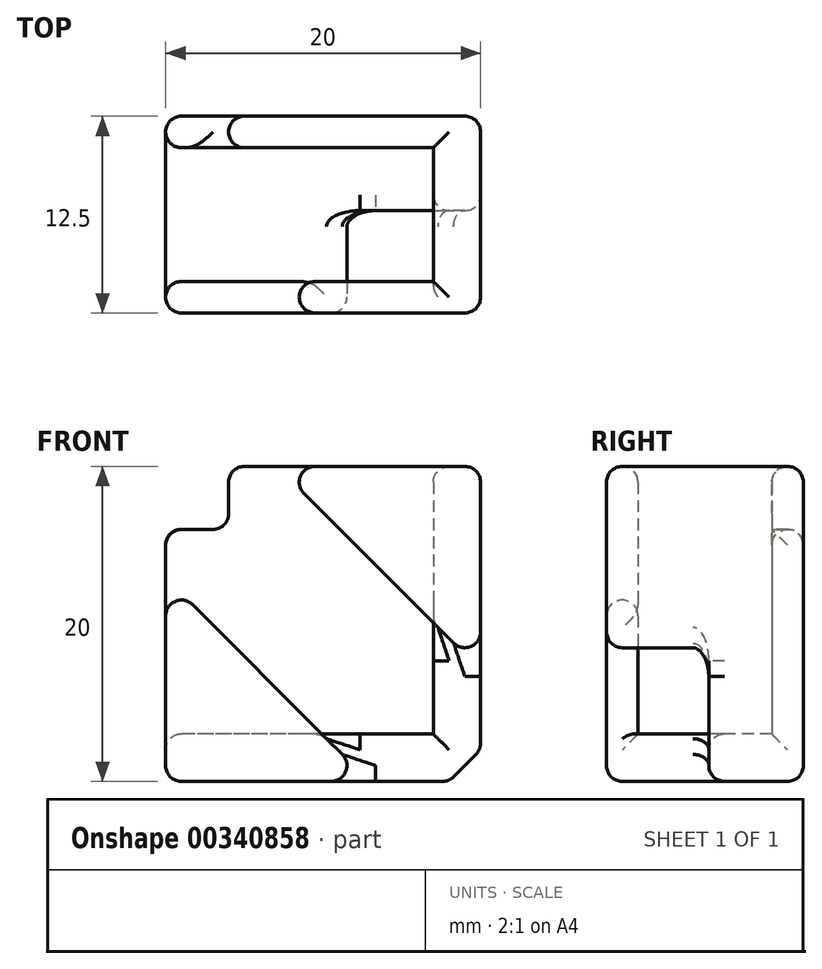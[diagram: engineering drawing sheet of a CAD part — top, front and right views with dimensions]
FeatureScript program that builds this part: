
annotation { "Feature Type Name" : "Feature", "Feature Type Description" : "" }
export const myFeature = defineFeature(function(context is Context, id is Id, definition is map)
    precondition{}
    {
        {
            var Q0;
            Q0=qCreatedBy(makeId("Top.planeOp"),FACE);
            var sketch = newSketch(context, id + "F0", { "sketchPlane" : qUnion([Q0])});
            skLineSegment(sketch, "E0.bottom", {"start": v(0, 0) * mm, "end": v(20, 0) * mm});
            skLineSegment(sketch, "E0.top", {"start": v(0, -12.5) * mm, "end": v(20, -12.5) * mm});
            skLineSegment(sketch, "E0.left", {"start": v(0, 0) * mm, "end": v(0, -12.5) * mm});
            skLineSegment(sketch, "E0.right", {"start": v(20, 0) * mm, "end": v(20, -12.5) * mm});
            skLineSegment(sketch, "E1.bottom", {"start": v(0, -2) * mm, "end": v(20, -2) * mm});
            skLineSegment(sketch, "E1.top", {"start": v(0, -10.5) * mm, "end": v(20, -10.5) * mm});
            skLineSegment(sketch, "E1.left", {"start": v(0, -2) * mm, "end": v(0, -10.5) * mm});
            skLineSegment(sketch, "E1.right", {"start": v(20, -2) * mm, "end": v(20, -10.5) * mm});
            skSolve(sketch);
        }
        {
            var Q0;
            Q0=qSketchRegion(id+"F0",true);
            extrude(context, id + "F1", {"entities" : qUnion([Q0]), "depth" : 3 * mm});
        }
        {
            var Q0;
            {var subQ0=sQuery(id+"F0.wireOp",EDGE,"E0.bottom");Q0=makeQuery(id+"F0.imprint","IMPRINT",FACE,{"disambiguationData":[TD([[makeQuery(id+"F0.imprint","IMPRINT",EDGE,{"derivedFrom":subQ0}),-1.0]])]});}
            var Q1;
            {var subQ0=sQuery(id+"F0.wireOp",EDGE,"E0.top");Q1=makeQuery(id+"F0.imprint","IMPRINT",FACE,{"disambiguationData":[TD([[makeQuery(id+"F0.imprint","IMPRINT",EDGE,{"derivedFrom":subQ0}),1.0]])]});}
            extrude(context, id + "F2", {"entities" : qUnion([Q0, Q1]), "operationType" : NewBodyOperationType.ADD, "depth" : 16 * mm});
        }
        {
            var Q0;
            Q0=makeQuery(id+"F1.opExtrude","SWEPT_BODY",BODY,{"disambiguationData":[OSD([sQuery(id+"F0.wireOp",EDGE,"E0.bottom"),sQuery(id+"F0.wireOp",EDGE,"E0.top"),sQuery(id+"F0.wireOp",EDGE,"E0.left"),sQuery(id+"F0.wireOp",EDGE,"E0.right"),sQuery(id+"F0.wireOp",EDGE,"E1.left"),sQuery(id+"F0.wireOp",EDGE,"E1.right")])]});
            var Q1;
            Q1=sQuery(id+"F0.wireOp",EDGE,"E1.left");
            transform(context, id + "F3", {"entities" : qUnion([Q0]), "transformType" : TransformType.ROTATION, "transformAxis" : qUnion([Q1]), "angle" : 90 * degree, "makeCopy" : true});
        }
        {
            var Q0;
            Q0=makeQuery(id+"F3.opPattern","COPY",BODY,{"derivedFrom":makeQuery(id+"F1.opExtrude","SWEPT_BODY",BODY,{"disambiguationData":[OSD([sQuery(id+"F0.wireOp",EDGE,"E0.bottom"),sQuery(id+"F0.wireOp",EDGE,"E0.top"),sQuery(id+"F0.wireOp",EDGE,"E0.left"),sQuery(id+"F0.wireOp",EDGE,"E0.right"),sQuery(id+"F0.wireOp",EDGE,"E1.left"),sQuery(id+"F0.wireOp",EDGE,"E1.right")])]}),"instanceName":"1"});
            var Q1;
            {var subQ0=sQuery(id+"F0.wireOp",EDGE,"E0.bottom");Q1=makeQuery(id+"FWMDLX0BPGAaUFk_1.opFillet","BLEND_EDGE",EDGE,{"blendedFrom":[makeQuery(id+"F1.opExtrude","CAP_EDGE",EDGE,{"disambiguationData":[OSD([subQ0])],"isStart":true}),makeQuery(id+"F1.opExtrude","CAP_FACE",FACE,{"disambiguationData":[OSD([subQ0,sQuery(id+"F0.wireOp",EDGE,"E0.top"),sQuery(id+"F0.wireOp",EDGE,"E0.left"),sQuery(id+"F0.wireOp",EDGE,"E0.right"),sQuery(id+"F0.wireOp",EDGE,"E1.left"),sQuery(id+"F0.wireOp",EDGE,"E1.right")])],"isStart":true})],"blendedInto":[makeQuery(id+"F1.opExtrude","CAP_FACE",FACE,{"disambiguationData":[OSD([subQ0,sQuery(id+"F0.wireOp",EDGE,"E0.top"),sQuery(id+"F0.wireOp",EDGE,"E0.left"),sQuery(id+"F0.wireOp",EDGE,"E0.right"),sQuery(id+"F0.wireOp",EDGE,"E1.left"),sQuery(id+"F0.wireOp",EDGE,"E1.right")])],"isStart":true})]});}
            transform(context, id + "F4", {"entities" : qUnion([Q0]), "transformType" : TransformType.TRANSLATION_3D, "dx" : 20 * mm, "dy" : 0 * mm, "dz" : 0 * mm, "makeCopy" : false});
        }
        {
            var Q0;
            Q0=makeQuery(id+"F1.opExtrude","SWEPT_BODY",BODY,{"disambiguationData":[OSD([sQuery(id+"F0.wireOp",EDGE,"E0.bottom"),sQuery(id+"F0.wireOp",EDGE,"E0.top"),sQuery(id+"F0.wireOp",EDGE,"E0.left"),sQuery(id+"F0.wireOp",EDGE,"E0.right"),sQuery(id+"F0.wireOp",EDGE,"E1.left"),sQuery(id+"F0.wireOp",EDGE,"E1.right")])]});
            var Q1;
            Q1=makeQuery(id+"F3.opPattern","COPY",BODY,{"derivedFrom":makeQuery(id+"F1.opExtrude","SWEPT_BODY",BODY,{"disambiguationData":[OSD([sQuery(id+"F0.wireOp",EDGE,"E0.bottom"),sQuery(id+"F0.wireOp",EDGE,"E0.top"),sQuery(id+"F0.wireOp",EDGE,"E0.left"),sQuery(id+"F0.wireOp",EDGE,"E0.right"),sQuery(id+"F0.wireOp",EDGE,"E1.left"),sQuery(id+"F0.wireOp",EDGE,"E1.right")])]}),"instanceName":"1"});
            booleanBodies(context, id + "F5", {"operationType" : BooleanOperationType.UNION, "tools" : qUnion([Q0, Q1])});
        }
        {
            var Q0;
            {var subQ0=sQuery(id+"F0.wireOp",EDGE,"E0.top");var subQ1=makeQuery(id+"F2.boolean.opBoolean","MERGE",FACE,{"derivedFrom":[makeQuery(id+"F1.opExtrude","SWEPT_FACE",FACE,{"disambiguationData":[OSD([subQ0])]}),makeQuery(id+"F2.opExtrude","SWEPT_FACE",FACE,{"disambiguationData":[OSD([subQ0])]})]});Q0=makeQuery(id+"F5.opBoolean","MERGE",FACE,{"derivedFrom":[subQ1,makeQuery(id+"F3.opPattern","COPY",FACE,{"derivedFrom":subQ1,"instanceName":"1"})]});}
            var sketch = newSketch(context, id + "F6", { "sketchPlane" : qUnion([Q0])});
            skPoint(sketch, "E2", {"position": v(10, 1) * mm});
            skPoint(sketch, "E3", {"position": v(19, 10) * mm});
            skLineSegment(sketch, "E4", {"start": v(3.97, 23.1) * mm, "end": v(-3.1, 16.03) * mm});
            skLineSegment(sketch, "E5", {"start": v(17.25, -4.32) * mm, "end": v(24.32, 2.75) * mm});
            skLineSegment(sketch, "E6", {"start": v(17.25, -4.32) * mm, "end": v(-3.1, 16.03) * mm});
            skLineSegment(sketch, "E7", {"start": v(24.32, 2.75) * mm, "end": v(3.97, 23.1) * mm});
            skSolve(sketch);
        }
        {
            var Q0;
            Q0 = qSketchRegion(id + "F6", true);
            extrude(context, id + "F7", {"entities" : qUnion([Q0]), "operationType" : NewBodyOperationType.REMOVE, "oppositeDirection" : true, "depth" : 6.5 * mm});
        }
        {
            var Q0;
            Q0=makeQuery(id+"F1.opExtrude","CAP_EDGE",EDGE,{"disambiguationData":[OSD([sQuery(id+"F0.wireOp",EDGE,"E0.right"),sQuery(id+"F0.wireOp",EDGE,"E1.right")])],"isStart":true});
            chamfer(context, id + "F8", {"entities" : qUnion([Q0]), "width" : 2 * mm, "tangentPropagation" : true});
        }
        {
            var Q0;
            {var subQ0=sQuery(id+"F0.wireOp",EDGE,"E0.bottom");var subQ1=makeQuery(id+"F2.boolean.opBoolean","MERGE",FACE,{"derivedFrom":[makeQuery(id+"F1.opExtrude","SWEPT_FACE",FACE,{"disambiguationData":[OSD([subQ0])]}),makeQuery(id+"F2.opExtrude","SWEPT_FACE",FACE,{"disambiguationData":[OSD([subQ0])]})]});Q0=makeQuery(id+"F5.opBoolean","MERGE",FACE,{"derivedFrom":[subQ1,makeQuery(id+"F3.opPattern","COPY",FACE,{"derivedFrom":subQ1,"instanceName":"1"})]});}
            var Q1;
            Q1=makeQuery(id+"F1.opExtrude","CAP_FACE",FACE,{"disambiguationData":[OSD([sQuery(id+"F0.wireOp",EDGE,"E0.bottom"),sQuery(id+"F0.wireOp",EDGE,"E0.top"),sQuery(id+"F0.wireOp",EDGE,"E0.left"),sQuery(id+"F0.wireOp",EDGE,"E0.right"),sQuery(id+"F0.wireOp",EDGE,"E1.left"),sQuery(id+"F0.wireOp",EDGE,"E1.right")])],"isStart":true});
            var Q2;
            {var subQ0=sQuery(id+"F0.wireOp",EDGE,"E1.right");var subQ1=sQuery(id+"F0.wireOp",EDGE,"E0.right");var subQ2=sQuery(id+"F0.wireOp",EDGE,"E0.top");var subQ3=sQuery(id+"F0.wireOp",EDGE,"E0.bottom");Q2=makeQuery(id+"F5.opBoolean","MERGE",FACE,{"derivedFrom":[makeQuery(id+"F2.boolean.opBoolean","MERGE",FACE,{"derivedFrom":[makeQuery(id+"F1.opExtrude","SWEPT_FACE",FACE,{"disambiguationData":[OSD([subQ1,subQ0])]}),makeQuery(id+"F2.opExtrude","SWEPT_FACE",FACE,{"disambiguationData":[OSD([subQ1]),TDD([makeQuery(id+"F0.imprint","IMPRINT",EDGE,{"disambiguationData":[TD([[makeQuery(id+"F0.imprint","INTERSECT",VERTEX,{"derivedFrom":[subQ3,subQ1]}),-1.0]])],"derivedFrom":subQ1})])]}),makeQuery(id+"F2.opExtrude","SWEPT_FACE",FACE,{"disambiguationData":[OSD([subQ1]),TDD([makeQuery(id+"F0.imprint","IMPRINT",EDGE,{"disambiguationData":[TD([[makeQuery(id+"F0.imprint","INTERSECT",VERTEX,{"derivedFrom":[subQ2,subQ1]}),1.0]])],"derivedFrom":subQ1})])]})]}),makeQuery(id+"F3.opPattern","COPY",FACE,{"derivedFrom":makeQuery(id+"F1.opExtrude","CAP_FACE",FACE,{"disambiguationData":[OSD([subQ3,subQ2,sQuery(id+"F0.wireOp",EDGE,"E0.left"),subQ1,sQuery(id+"F0.wireOp",EDGE,"E1.left"),subQ0])],"isStart":true}),"instanceName":"1"})]});}
            var Q3;
            Q3=makeQuery(id+"F7.boolean.opBoolean","COPY",FACE,{"derivedFrom":makeQuery(id+"F7.opExtrude","CAP_FACE",FACE,{"disambiguationData":[OSD([sQuery(id+"F6.wireOp",EDGE,"E4"),sQuery(id+"F6.wireOp",EDGE,"E5"),sQuery(id+"F6.wireOp",EDGE,"E6"),sQuery(id+"F6.wireOp",EDGE,"E7")])],"isStart":false})});
            var Q4;
            Q4=makeQuery(id+"F7.boolean.opBoolean","COPY",FACE,{"derivedFrom":makeQuery(id+"F7.opExtrude","SWEPT_FACE",FACE,{"disambiguationData":[OSD([sQuery(id+"F6.wireOp",EDGE,"E6")])]})});
            var Q5;
            {var subQ0=sQuery(id+"F0.wireOp",EDGE,"E0.left");var subQ1=sQuery(id+"F0.wireOp",EDGE,"E1.left");Q5=makeQuery(id+"F2.boolean.opBoolean","MERGE",FACE,{"derivedFrom":[makeQuery(id+"F1.opExtrude","SWEPT_FACE",FACE,{"disambiguationData":[OSD([subQ0,subQ1])]}),makeQuery(id+"F2.opExtrude","SWEPT_FACE",FACE,{"disambiguationData":[OSD([subQ0]),TDD([makeQuery(id+"F0.imprint","IMPRINT",EDGE,{"disambiguationData":[TD([[makeQuery(id+"F0.imprint","INTERSECT",VERTEX,{"derivedFrom":[sQuery(id+"F0.wireOp",EDGE,"E0.bottom"),subQ0]}),-1.0]])],"derivedFrom":subQ0})])]}),makeQuery(id+"F2.opExtrude","SWEPT_FACE",FACE,{"disambiguationData":[OSD([subQ0]),TDD([makeQuery(id+"F0.imprint","IMPRINT",EDGE,{"disambiguationData":[TD([[makeQuery(id+"F0.imprint","INTERSECT",VERTEX,{"derivedFrom":[sQuery(id+"F0.wireOp",EDGE,"E0.top"),subQ0]}),1.0]])],"derivedFrom":subQ0})])]})]});}
            var Q6;
            {var subQ0=sQuery(id+"F0.wireOp",EDGE,"E0.right");var subQ1=sQuery(id+"F0.wireOp",EDGE,"E1.right");Q6=makeQuery(id+"F3.opPattern","COPY",FACE,{"derivedFrom":makeQuery(id+"F2.boolean.opBoolean","MERGE",FACE,{"derivedFrom":[makeQuery(id+"F1.opExtrude","SWEPT_FACE",FACE,{"disambiguationData":[OSD([subQ0,subQ1])]}),makeQuery(id+"F2.opExtrude","SWEPT_FACE",FACE,{"disambiguationData":[OSD([subQ0]),TDD([makeQuery(id+"F0.imprint","IMPRINT",EDGE,{"disambiguationData":[TD([[makeQuery(id+"F0.imprint","INTERSECT",VERTEX,{"derivedFrom":[sQuery(id+"F0.wireOp",EDGE,"E0.bottom"),subQ0]}),-1.0]])],"derivedFrom":subQ0})])]}),makeQuery(id+"F2.opExtrude","SWEPT_FACE",FACE,{"disambiguationData":[OSD([subQ0]),TDD([makeQuery(id+"F0.imprint","IMPRINT",EDGE,{"disambiguationData":[TD([[makeQuery(id+"F0.imprint","INTERSECT",VERTEX,{"derivedFrom":[sQuery(id+"F0.wireOp",EDGE,"E0.top"),subQ0]}),1.0]])],"derivedFrom":subQ0})])]})]}),"instanceName":"1"});}
            var Q7;
            Q7=makeQuery(id+"F7.boolean.opBoolean","COPY",FACE,{"derivedFrom":makeQuery(id+"F7.opExtrude","SWEPT_FACE",FACE,{"disambiguationData":[OSD([sQuery(id+"F6.wireOp",EDGE,"E7")])]})});
            var Q8;
            Q8=makeQuery(id+"F3.opPattern","COPY",FACE,{"derivedFrom":makeQuery(id+"F2.opExtrude","CAP_FACE",FACE,{"disambiguationData":[OSD([sQuery(id+"F0.wireOp",EDGE,"E0.bottom"),sQuery(id+"F0.wireOp",EDGE,"E0.left"),sQuery(id+"F0.wireOp",EDGE,"E0.right"),sQuery(id+"F0.wireOp",EDGE,"E1.bottom")])],"isStart":false}),"instanceName":"1"});
            fillet(context, id + "F9", {"entities" : qUnion([Q0, Q1, Q2, Q3, Q4, Q5, Q6, Q7, Q8]), "radius" : 1 * mm, "tangentPropagation" : true, "allowEdgeOverflow" : false});
        }
    });
